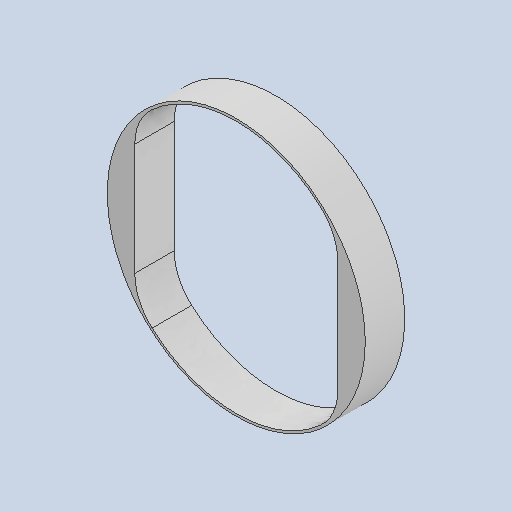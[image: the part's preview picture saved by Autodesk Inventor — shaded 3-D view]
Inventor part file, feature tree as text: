
AUTODESK INVENTOR PART (.ipt)
format: ipt  version: 2022 (Build 260153000, 153)  size: 114,176 bytes
history: native  units: in
note: dims shown in document units (in); Inventor stores cm internally (conversion verified against a paired STEP export)
features: other x3, sketch x1, plane x1
ambient origin geometry x8: Origin, YZ Plane, XZ Plane, XY Plane, X Axis, Y Axis, Z Axis, Center Point
bodies: Solid1 (feature_tree)
feature tree (5):
  other  "encoderring.ipt"
  other  "Solid1::encoderring.ipt"
  other  "TaggingFeature1"
  sketch  "Sketch1"  dims[d0=0.3937in]
  plane  "Work Plane1"
